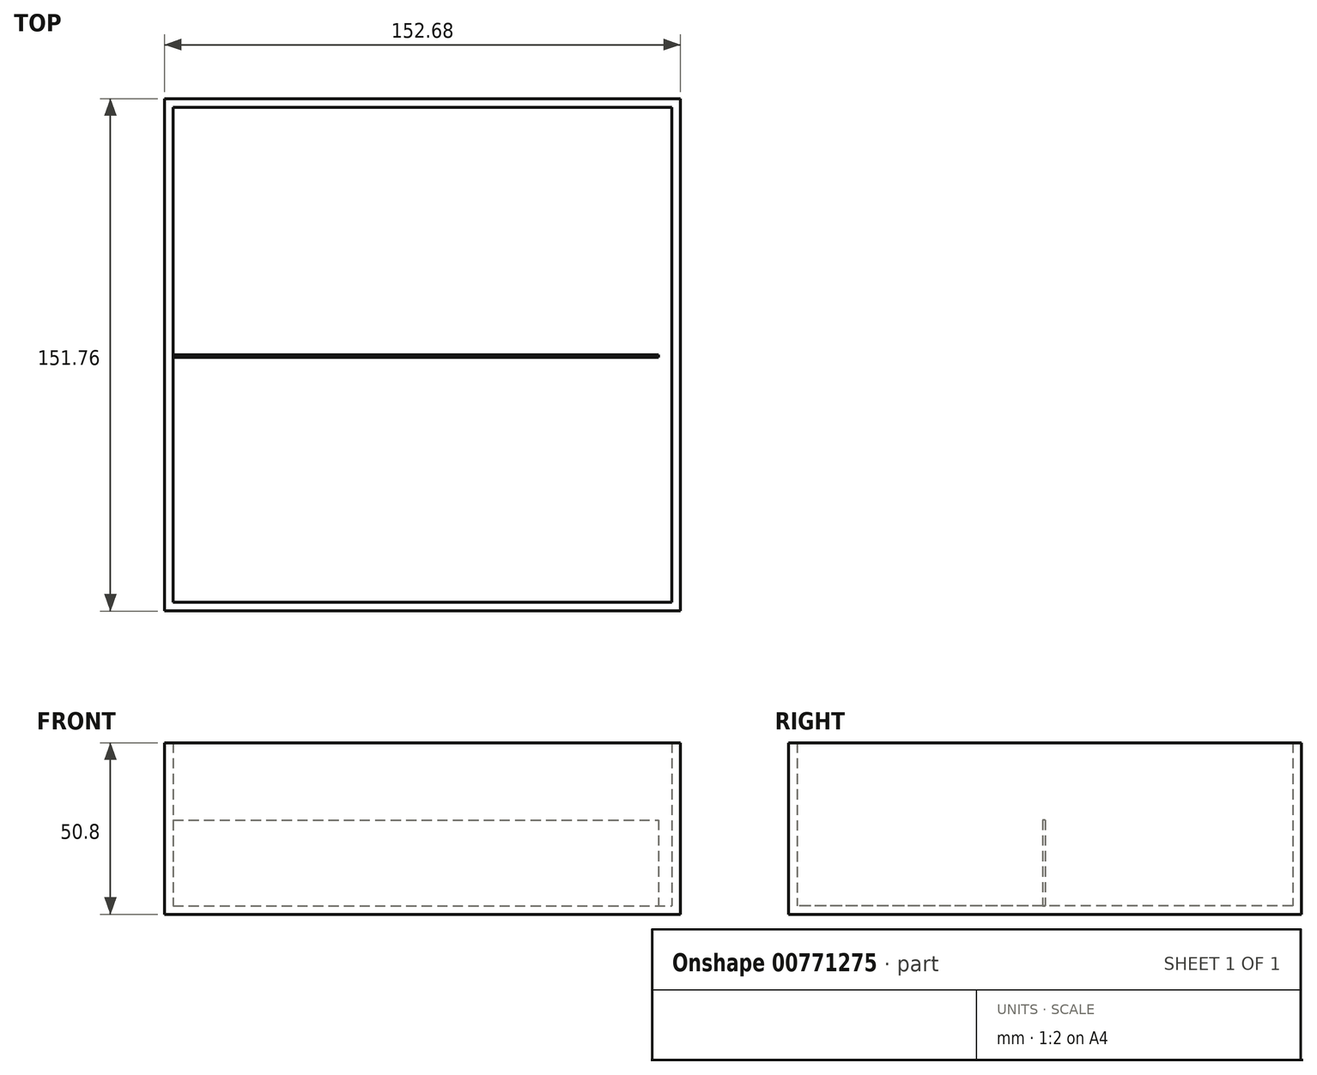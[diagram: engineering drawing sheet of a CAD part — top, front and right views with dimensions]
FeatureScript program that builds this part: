
annotation { "Feature Type Name" : "Feature", "Feature Type Description" : "" }
export const myFeature = defineFeature(function(context is Context, id is Id, definition is map)
    precondition{}
    {
        {
            var Q0;
            Q0=qCreatedBy(makeId("Top.planeOp"),FACE);
            var sketch = newSketch(context, id + "F0", { "sketchPlane" : qUnion([Q0])});
            skLineSegment(sketch, "E0.bottom", {"start": v(-76.55, 76.64) * mm, "end": v(76.13, 76.64) * mm});
            skLineSegment(sketch, "E0.top", {"start": v(-76.55, -75.12) * mm, "end": v(76.13, -75.12) * mm});
            skLineSegment(sketch, "E0.left", {"start": v(-76.55, 76.64) * mm, "end": v(-76.55, -75.12) * mm});
            skLineSegment(sketch, "E0.right", {"start": v(76.13, 76.64) * mm, "end": v(76.13, -75.12) * mm});
            skSolve(sketch);
        }
        {
            var Q0;
            Q0 = qSketchRegion(id + "F0", true);
            extrude(context, id + "F1", {"entities" : qUnion([Q0]), "depth" : 25.4 * mm, "offsetDistance" : 25.4 * mm});
        }
        {
            var Q0;
            Q0=makeQuery(id+"F1.opExtrude","CAP_FACE",FACE,{"disambiguationData":[OSD([sQuery(id+"F0.wireOp",EDGE,"E0.bottom"),sQuery(id+"F0.wireOp",EDGE,"E0.top"),sQuery(id+"F0.wireOp",EDGE,"E0.left"),sQuery(id+"F0.wireOp",EDGE,"E0.right")])],"isStart":false});
            extrude(context, id + "F2", {"entities" : qUnion([Q0]), "operationType" : NewBodyOperationType.ADD, "depth" : 25.4 * mm, "offsetDistance" : 25.4 * mm});
        }
        {
            var Q0;
            Q0=makeQuery(id+"F2.opExtrude","CAP_FACE",FACE,{"disambiguationData":[OSD([sQuery(id+"F0.wireOp",EDGE,"E0.bottom"),sQuery(id+"F0.wireOp",EDGE,"E0.top"),sQuery(id+"F0.wireOp",EDGE,"E0.left"),sQuery(id+"F0.wireOp",EDGE,"E0.right")])],"isStart":false});
            shell(context, id + "F3", {"entities" : qUnion([Q0]), "thickness" : 2.54 * mm});
        }
        {
            var Q0;
            Q0=makeQuery(id+"F3.opShell","OFFSET_FACE",FACE,{"disambiguationData":[OSD([sQuery(id+"F0.wireOp",EDGE,"E0.bottom"),sQuery(id+"F0.wireOp",EDGE,"E0.top"),sQuery(id+"F0.wireOp",EDGE,"E0.left"),sQuery(id+"F0.wireOp",EDGE,"E0.right")])]});
            var sketch = newSketch(context, id + "F4", { "sketchPlane" : qUnion([Q0])});
            skPoint(sketch, "E1.oppositeSnap0", {"position": v(73.59, 0.76) * mm});
            skLineSegment(sketch, "E1.bottom", {"start": v(-74.01, 0) * mm, "end": v(69.69, 0) * mm});
            skLineSegment(sketch, "E1.top", {"start": v(-74.01, 0.76) * mm, "end": v(69.69, 0.76) * mm});
            skLineSegment(sketch, "E1.left", {"start": v(-74.01, 0) * mm, "end": v(-74.01, 0.76) * mm});
            skLineSegment(sketch, "E1.right", {"start": v(69.69, 0) * mm, "end": v(69.69, 0.76) * mm});
            skSolve(sketch);
        }
        {
            var Q0;
            Q0 = qSketchRegion(id + "F4", true);
            extrude(context, id + "F5", {"entities" : qUnion([Q0]), "operationType" : NewBodyOperationType.ADD, "depth" : 25.4 * mm, "offsetDistance" : 25.4 * mm});
        }
    });
